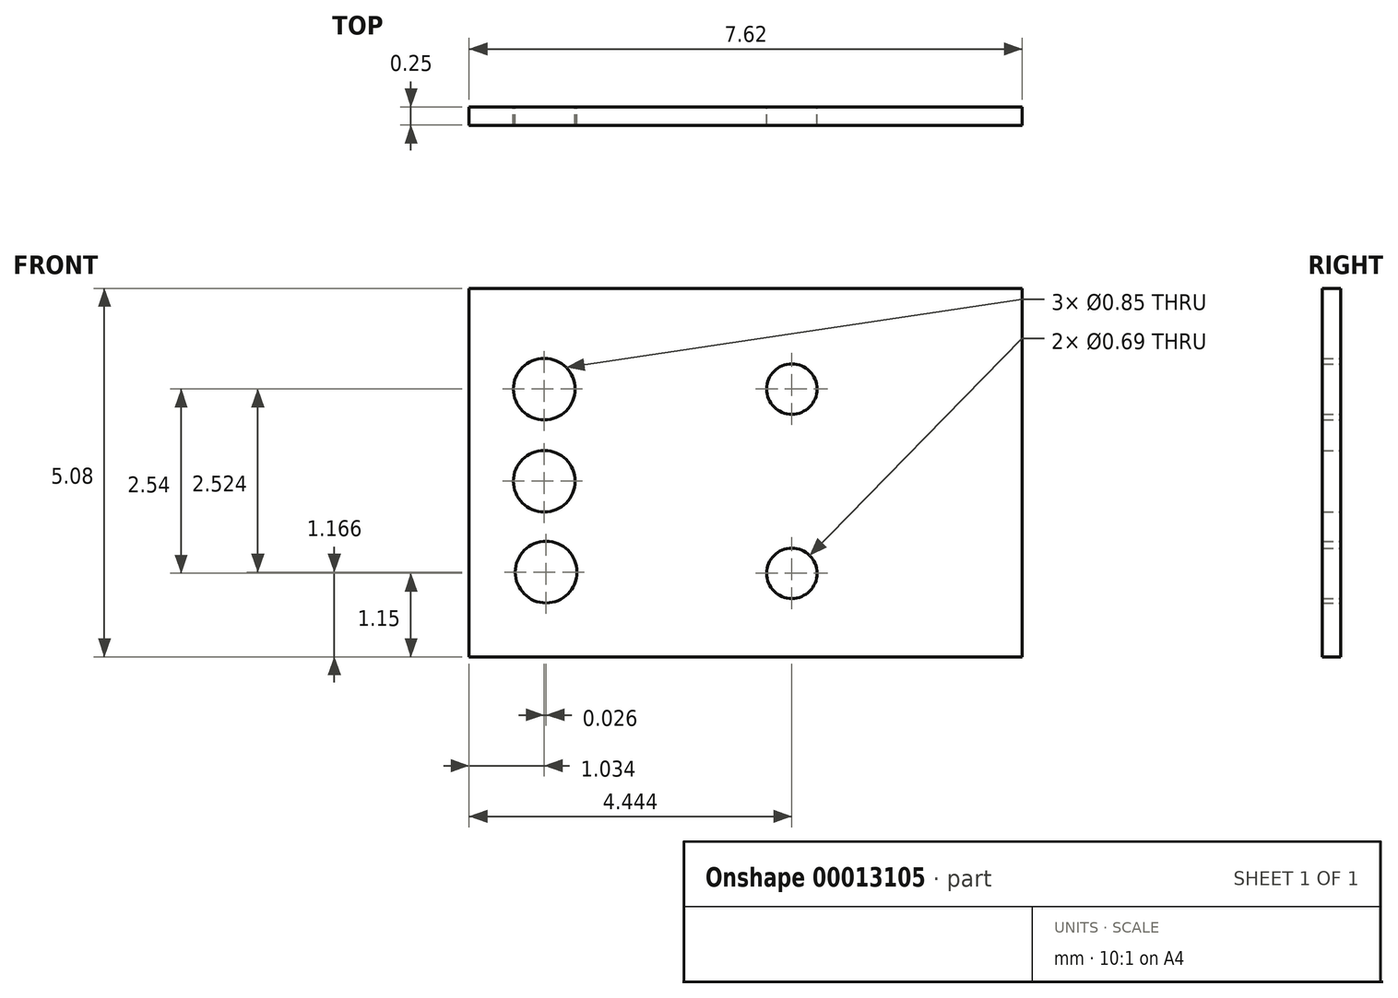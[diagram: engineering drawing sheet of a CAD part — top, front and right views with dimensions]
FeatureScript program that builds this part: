
annotation { "Feature Type Name" : "Feature", "Feature Type Description" : "" }
export const myFeature = defineFeature(function(context is Context, id is Id, definition is map)
    precondition{}
    {
        {
            var Q0;
            Q0=qCreatedBy(makeId("Front.planeOp"),FACE);
            var sketch = newSketch(context, id + "F0", { "sketchPlane" : qUnion([Q0])});
            skLineSegment(sketch, "E0", {"start": v(14.41, 0) * mm, "end": v(14.41, 1.27) * mm});
            skLineSegment(sketch, "E1", {"start": v(14.41, 0) * mm, "end": v(14.41, -1.27) * mm});
            skCircle(sketch, "E2", {"center": v(14.41, 1.27) * mm, "radius": 0.35 * mm});
            skCircle(sketch, "E3", {"center": v(14.41, -1.27) * mm, "radius": 0.35 * mm});
            skLineSegment(sketch, "E4", {"start": v(14.41, -1.27) * mm, "end": v(11, -1.27) * mm});
            skLineSegment(sketch, "E5", {"start": v(14.41, 1.27) * mm, "end": v(11, 1.27) * mm});
            skCircle(sketch, "E6", {"center": v(11, 1.27) * mm, "radius": 0.43 * mm});
            skCircle(sketch, "E7", {"center": v(11, 0) * mm, "radius": 0.43 * mm});
            skCircle(sketch, "E8", {"center": v(11.03, -1.25) * mm, "radius": 0.43 * mm});
            skLineSegment(sketch, "E9", {"start": v(11, 0) * mm, "end": v(13.64, 0) * mm});
            skLineSegment(sketch, "E10.bottom", {"start": v(17.6, 2.66) * mm, "end": v(9.97, 2.66) * mm});
            skLineSegment(sketch, "E10.top", {"start": v(17.6, -2.42) * mm, "end": v(9.97, -2.42) * mm});
            skLineSegment(sketch, "E10.left", {"start": v(17.6, 2.66) * mm, "end": v(17.6, -2.42) * mm});
            skLineSegment(sketch, "E10.right", {"start": v(9.97, 2.66) * mm, "end": v(9.97, -2.42) * mm});
            skSolve(sketch);
        }
        {
            var Q0;
            Q0=makeQuery(id+"F0.imprint","IMPRINT",FACE,{"disambiguationData":[TD([[makeQuery(id+"F0.imprint","IMPRINT",EDGE,{"derivedFrom":sQuery(id+"F0.wireOp",EDGE,"E6")}),-1.0]])]});
            extrude(context, id + "F1", {"entities" : qUnion([Q0]), "depth" : 0.25 * mm});
        }
    });
